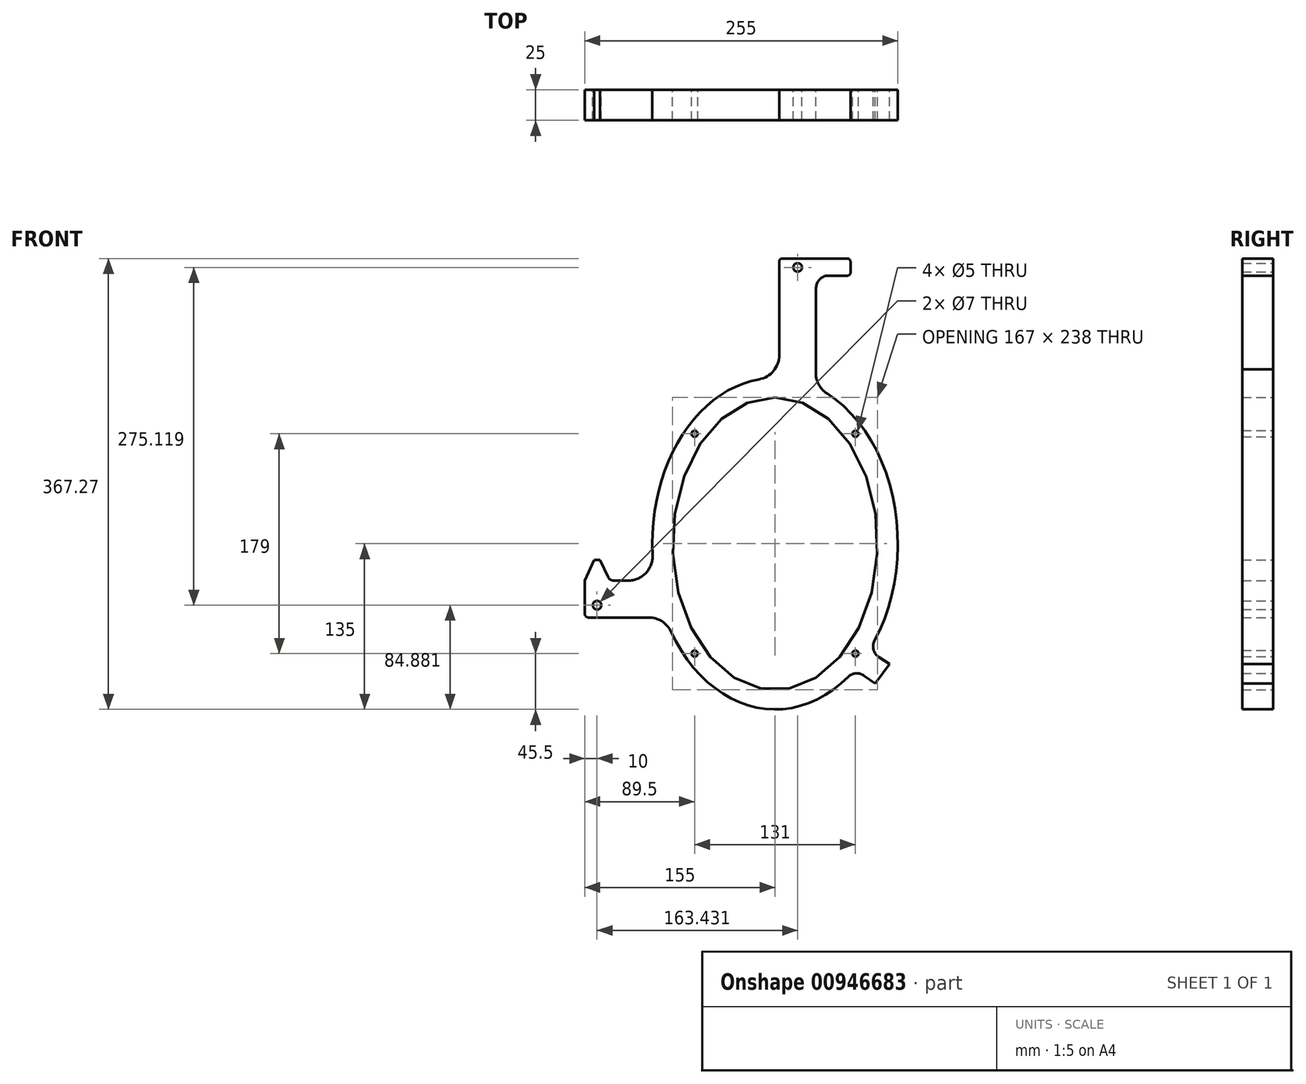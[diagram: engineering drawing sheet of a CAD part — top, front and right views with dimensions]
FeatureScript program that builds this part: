
annotation { "Feature Type Name" : "Feature", "Feature Type Description" : "" }
export const myFeature = defineFeature(function(context is Context, id is Id, definition is map)
    precondition{}
    {
        {
            var Q0;
            Q0=qCreatedBy(makeId("Front.planeOp"),FACE);
            var sketch = newSketch(context, id + "F0", { "sketchPlane" : qUnion([Q0])});
            skCircle(sketch, "E0", {"center": v(18.43, 225) * mm, "radius": 3.5 * mm});
            skCircle(sketch, "E1", {"center": v(-145, -50.12) * mm, "radius": 3.5 * mm});
            skEllipse(sketch, "E2", {"center": v(0, 0) * mm, "majorRadius": 119 * mm, "minorRadius": 83.5 * mm, "majorAxis": v(0, 1)});
            skEllipticalArc(sketch, "E3", {});
            skCircle(sketch, "E4", {"center": v(-65.5, 89.5) * mm, "radius": 2.5 * mm});
            skCircle(sketch, "E5", {"center": v(65.5, 89.5) * mm, "radius": 2.5 * mm});
            skCircle(sketch, "E6", {"center": v(-65.5, -89.5) * mm, "radius": 2.5 * mm});
            skCircle(sketch, "E7", {"center": v(65.5, -89.5) * mm, "radius": 2.5 * mm});
            skLineSegment(sketch, "E8", {"start": v(-65.5, 89.5) * mm, "end": v(65.5, 89.5) * mm, "construction": true});
            skLineSegment(sketch, "E9", {"start": v(0, 0) * mm, "end": v(0, 89.5) * mm, "construction": true});
            skLineSegment(sketch, "E10", {"start": v(-65.5, 89.5) * mm, "end": v(-65.5, -89.5) * mm, "construction": true});
            skLineSegment(sketch, "E11", {"start": v(-65.5, -89.5) * mm, "end": v(65.5, -89.5) * mm, "construction": true});
            skLineSegment(sketch, "E12", {"start": v(65.5, -89.5) * mm, "end": v(65.5, 89.5) * mm, "construction": true});
            skLineSegment(sketch, "E13", {"start": v(0, 135) * mm, "end": v(-280.04, 135) * mm, "construction": true});
            skLineSegment(sketch, "E14", {"start": v(-100, 0) * mm, "end": v(-100, 135) * mm, "construction": true});
            skLineSegment(sketch, "E15", {"start": v(18.43, 225) * mm, "end": v(18.43, 135) * mm, "construction": true});
            skLineSegment(sketch, "E16", {"start": v(-145, -50.12) * mm, "end": v(-100, -50.12) * mm, "construction": true});
            skLineSegment(sketch, "E17", {"start": v(18.43, 225) * mm, "end": v(-145, -50.12) * mm, "construction": true});
            skLineSegment(sketch, "E18", {"start": v(3.43, 229.77) * mm, "end": v(3.43, 153.53) * mm});
            skLineSegment(sketch, "E19", {"start": v(5.93, 232.27) * mm, "end": v(33.43, 232.27) * mm});
            skLineSegment(sketch, "E20", {"start": v(-119.75, -30.12) * mm, "end": v(-131.43, -30.12) * mm});
            skLineSegment(sketch, "E21", {"start": v(-152, -60.12) * mm, "end": v(-102.87, -60.12) * mm});
            skLineSegment(sketch, "E22", {"start": v(84.43, -92.16) * mm, "end": v(93.24, -97.89) * mm});
            skLineSegment(sketch, "E23", {"start": v(93.24, -97.89) * mm, "end": v(81.45, -114.04) * mm});
            skLineSegment(sketch, "E24", {"start": v(81.45, -114.04) * mm, "end": v(72.48, -107.49) * mm});
            skLineSegment(sketch, "E25", {"start": v(18.43, 225) * mm, "end": v(45.43, 225) * mm, "construction": true});
            skCircle(sketch, "E26", {"center": v(45.43, 225) * mm, "radius": 5 * mm});
            skLineSegment(sketch, "E27", {"start": v(33.43, 232.27) * mm, "end": v(58.93, 232.27) * mm});
            skLineSegment(sketch, "E28", {"start": v(61.43, 229.77) * mm, "end": v(61.43, 220.74) * mm});
            skLineSegment(sketch, "E29", {"start": v(58.93, 218.24) * mm, "end": v(43.43, 218.24) * mm});
            skLineSegment(sketch, "E30", {"start": v(45.43, 225) * mm, "end": v(61.43, 225) * mm, "construction": true});
            skLineSegment(sketch, "E31", {"start": v(18.43, 225) * mm, "end": v(18.43, 232.27) * mm, "construction": true});
            skLineSegment(sketch, "E32", {"start": v(-145, -50.12) * mm, "end": v(-145, -28.12) * mm, "construction": true});
            skLineSegment(sketch, "E33", {"start": v(-147.5, -28.12) * mm, "end": v(-142.5, -28.12) * mm});
            skLineSegment(sketch, "E34", {"start": v(-147.5, -28.12) * mm, "end": v(-147.5, -13.12) * mm});
            skLineSegment(sketch, "E35", {"start": v(-147.5, -13.12) * mm, "end": v(-142.5, -13.12) * mm});
            skLineSegment(sketch, "E36", {"start": v(-142.5, -28.12) * mm, "end": v(-142.5, -13.12) * mm});
            skLineSegment(sketch, "E37", {"start": v(-147.5, -28.12) * mm, "end": v(-147.5, -30.12) * mm});
            skLineSegment(sketch, "E38", {"start": v(-142.5, -28.12) * mm, "end": v(-142.5, -30.12) * mm});
            skLineSegment(sketch, "E39", {"start": v(-147.5, -13.12) * mm, "end": v(-155, -30.12) * mm});
            skLineSegment(sketch, "E40", {"start": v(-142.5, -13.12) * mm, "end": v(-135.96, -27.22) * mm});
            skPoint(sketch, "E41.visualSharp", {"position": v(28.43, 129.43) * mm});
            skArc(sketch, "E41.filletArc", {"start": v(33.43, 141.95) * mm, "mid": v(35.05, 130.73) * mm, "end": v(42.51, 122.2) * mm});
            skPoint(sketch, "E42.visualSharp", {"position": v(3.43, 134.92) * mm});
            skArc(sketch, "E42.filletArc", {"start": v(-13.07, 133.84) * mm, "mid": v(-1.24, 140.69) * mm, "end": v(3.43, 153.53) * mm});
            skEllipticalArc(sketch, "E43.trimOffspring", {});
            skPoint(sketch, "E44.visualSharp", {"position": v(-97.48, -30.12) * mm});
            skArc(sketch, "E44.filletArc", {"start": v(-119.75, -30.12) * mm, "mid": v(-105.25, -23.9) * mm, "end": v(-99.77, -9.12) * mm});
            skPoint(sketch, "E45.visualSharp", {"position": v(-89.54, -60.12) * mm});
            skArc(sketch, "E45.filletArc", {"start": v(-84.73, -71.7) * mm, "mid": v(-92.11, -63.26) * mm, "end": v(-102.87, -60.12) * mm});
            skLineSegment(sketch, "E46.trimOffspring", {"start": v(-142.5, -30.12) * mm, "end": v(-147.5, -30.12) * mm});
            skPoint(sketch, "E47.visualSharp", {"position": v(-134.62, -30.12) * mm});
            skArc(sketch, "E47.filletArc", {"start": v(-135.96, -27.22) * mm, "mid": v(-134.12, -29.33) * mm, "end": v(-131.43, -30.12) * mm});
            skPoint(sketch, "E48.visualSharp", {"position": v(61.43, 232.27) * mm});
            skArc(sketch, "E48.filletArc", {"start": v(61.43, 229.77) * mm, "mid": v(60.7, 231.54) * mm, "end": v(58.93, 232.27) * mm});
            skPoint(sketch, "E49.visualSharp", {"position": v(61.43, 218.24) * mm});
            skArc(sketch, "E49.filletArc", {"start": v(58.93, 218.24) * mm, "mid": v(60.7, 218.97) * mm, "end": v(61.43, 220.74) * mm});
            skPoint(sketch, "E50.visualSharp", {"position": v(3.43, 232.27) * mm});
            skArc(sketch, "E50.filletArc", {"start": v(5.93, 232.27) * mm, "mid": v(4.16, 231.54) * mm, "end": v(3.43, 229.77) * mm});
            skLineSegment(sketch, "E51.trimOffspring", {"start": v(33.43, 208.24) * mm, "end": v(33.43, 141.95) * mm});
            skPoint(sketch, "E52.visualSharp", {"position": v(33.43, 218.24) * mm});
            skArc(sketch, "E52.filletArc", {"start": v(43.43, 218.24) * mm, "mid": v(36.36, 215.31) * mm, "end": v(33.43, 208.24) * mm});
            skEllipticalArc(sketch, "E53.trimOffspring", {});
            skPoint(sketch, "E54.visualSharp", {"position": v(65.3, -102.25) * mm});
            skArc(sketch, "E54.filletArc", {"start": v(72.48, -107.49) * mm, "mid": v(65.8, -105.6) * mm, "end": v(59.5, -108.5) * mm});
            skPoint(sketch, "E55.visualSharp", {"position": v(76.47, -86.99) * mm});
            skArc(sketch, "E55.filletArc", {"start": v(81.06, -79.05) * mm, "mid": v(80.2, -86.26) * mm, "end": v(84.43, -92.16) * mm});
            skLineSegment(sketch, "E56", {"start": v(-145, -50.12) * mm, "end": v(-155, -50.12) * mm, "construction": true});
            skLineSegment(sketch, "E57", {"start": v(-155, -30.12) * mm, "end": v(-155, -50.12) * mm});
            skLineSegment(sketch, "E58", {"start": v(-152, -60.12) * mm, "end": v(-152, -60.12) * mm});
            skLineSegment(sketch, "E59", {"start": v(-155, -50.12) * mm, "end": v(-155, -57.12) * mm});
            skPoint(sketch, "E60.visualSharp", {"position": v(-155, -60.12) * mm});
            skArc(sketch, "E60.filletArc", {"start": v(-155, -57.12) * mm, "mid": v(-154.12, -59.24) * mm, "end": v(-152, -60.12) * mm});
            const initialGuessF0  = {"E3": [0, 0, 0, 1, 0.135, 0.1, 0.13103180311342622, 1.6383821885523928], "E43.trimOffspring": [0, 0, 0, 1, 0.135, 0.1, 2.130677004492344, 3.7789807423381663], "E53.trimOffspring": [0, 0, 0, 1, 0.135, 0.1, 4.086780578500191, 5.844072207990556]};
            skSetInitialGuess(sketch, initialGuessF0);
            skSolve(sketch);
        }
        {
            var Q0;
            Q0 = qSketchRegion(id + "F0", true);
            var Q1;
            Q1=makeQuery(id+"F0.imprint","IMPRINT",FACE,{"disambiguationData":[TD([[makeQuery(id+"F0.imprint","IMPRINT",EDGE,{"derivedFrom":sQuery(id+"F0.wireOp",EDGE,"E33")}),-1.0]])]});
            extrude(context, id + "F1", {"entities" : qUnion([Q0, Q1]), "depth" : 25 * mm, "offsetDistance" : 25 * mm});
        }
        {
            var Q0;
            Q0=makeQuery(id+"F0.imprint","IMPRINT",FACE,{"disambiguationData":[TD([[makeQuery(id+"F0.imprint","IMPRINT",EDGE,{"derivedFrom":sQuery(id+"F0.wireOp",EDGE,"E26")}),1.0]])]});
            extrude(context, id + "F2", {"entities" : qUnion([Q0]), "operationType" : NewBodyOperationType.ADD, "depth" : 25 * mm, "offsetDistance" : 25 * mm});
        }
    });
